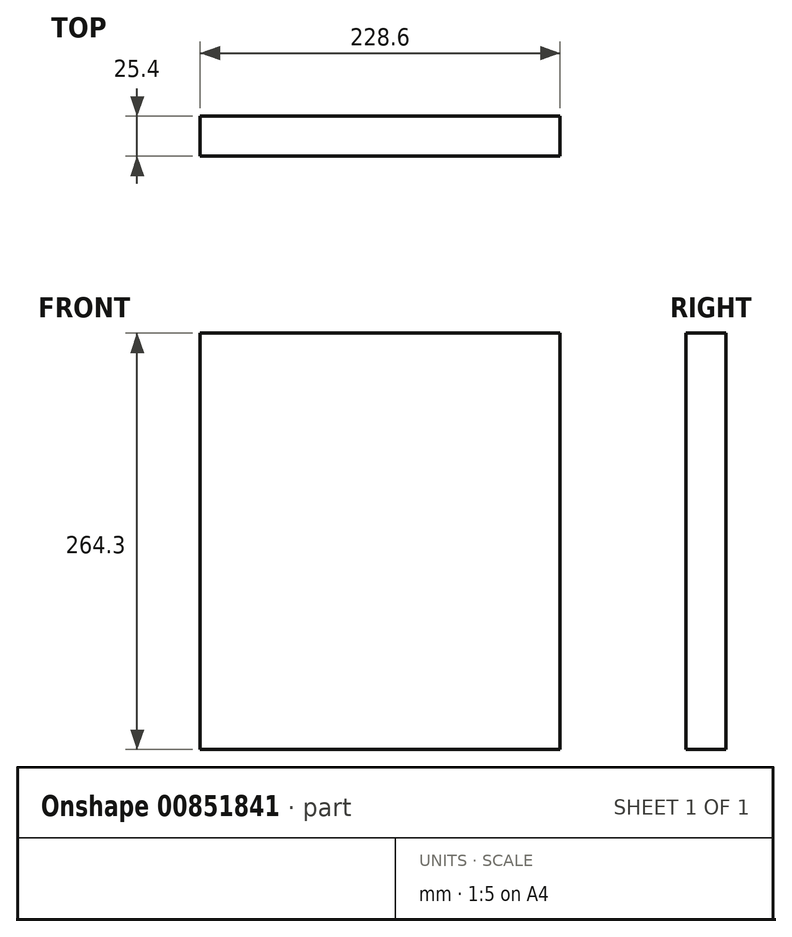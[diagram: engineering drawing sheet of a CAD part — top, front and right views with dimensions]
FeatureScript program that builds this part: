
annotation { "Feature Type Name" : "Feature", "Feature Type Description" : "" }
export const myFeature = defineFeature(function(context is Context, id is Id, definition is map)
    precondition{}
    {
        {
            var Q0;
            Q0=qCreatedBy(makeId("Front.planeOp"),FACE);
            var sketch = newSketch(context, id + "F0", { "sketchPlane" : qUnion([Q0])});
            skLineSegment(sketch, "E0.bottom", {"start": v(114.3, -132.15) * mm, "end": v(-114.3, -132.15) * mm});
            skLineSegment(sketch, "E0.top", {"start": v(114.3, 132.15) * mm, "end": v(-114.3, 132.15) * mm});
            skLineSegment(sketch, "E0.left", {"start": v(114.3, -132.15) * mm, "end": v(114.3, 132.15) * mm});
            skLineSegment(sketch, "E0.right", {"start": v(-114.3, -132.15) * mm, "end": v(-114.3, 132.15) * mm});
            skPoint(sketch, "E0.middle", {"position": v(0, 0) * mm});
            skSolve(sketch);
        }
        {
            var Q0;
            Q0=makeQuery(id+"F0.imprint","IMPRINT",FACE,{"disambiguationData":[TD([[makeQuery(id+"F0.imprint","IMPRINT",EDGE,{"derivedFrom":sQuery(id+"F0.wireOp",EDGE,"E0.bottom")}),-1.0]])]});
            extrude(context, id + "F1", {"entities" : qUnion([Q0]), "depth" : 25.4 * mm, "offsetDistance" : 25.4 * mm});
        }
    });
